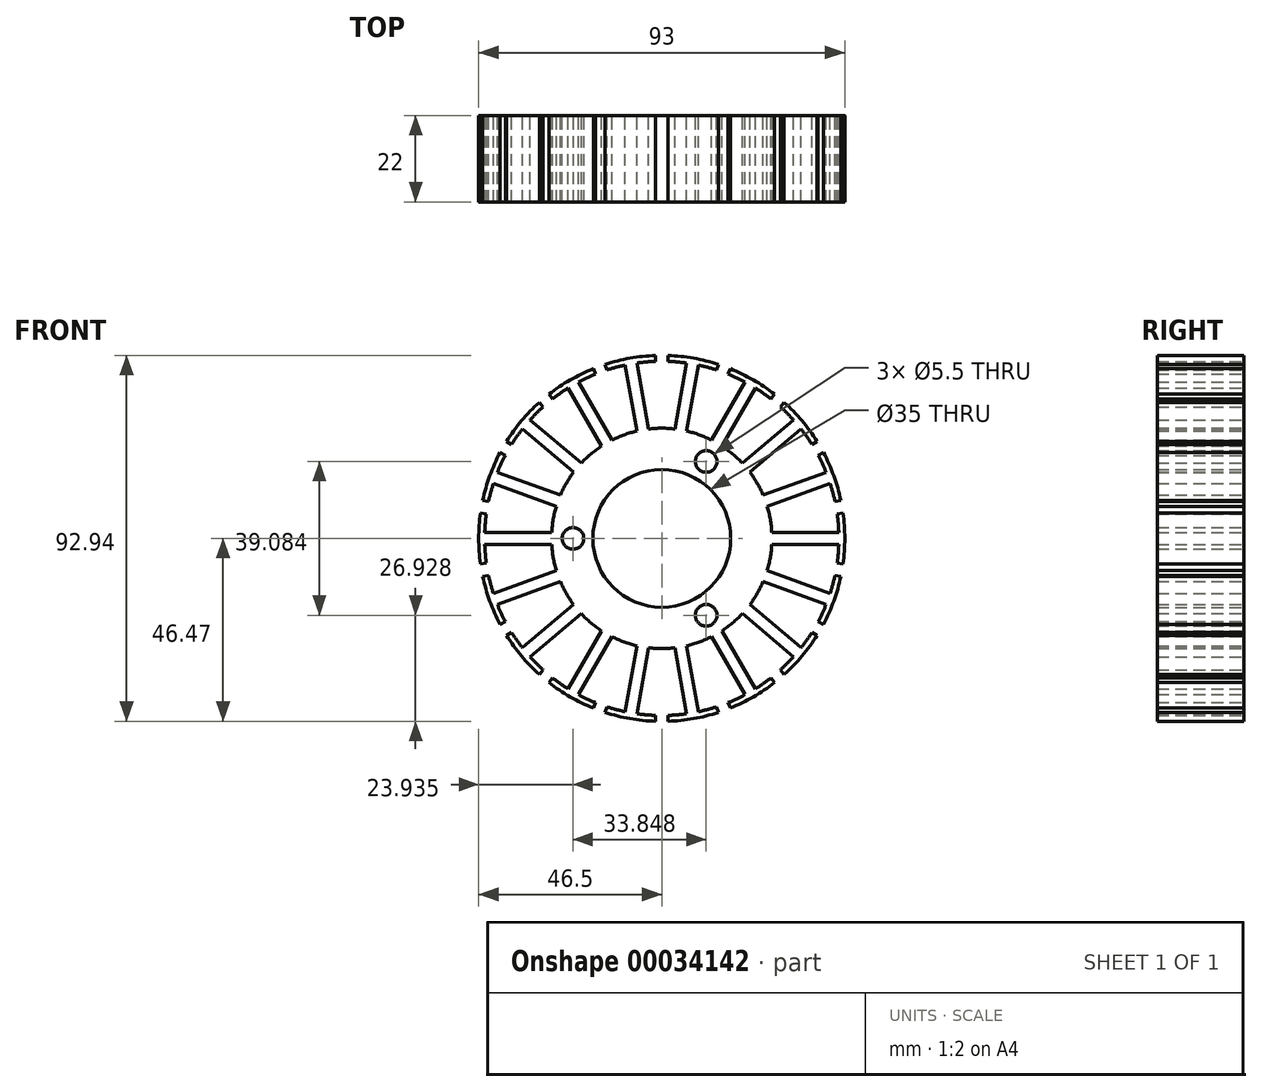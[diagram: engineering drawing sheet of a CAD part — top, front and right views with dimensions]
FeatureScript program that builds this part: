
annotation { "Feature Type Name" : "Feature", "Feature Type Description" : "" }
export const myFeature = defineFeature(function(context is Context, id is Id, definition is map)
    precondition{}
    {
        {
            var Q0;
            Q0=qCreatedBy(makeId("Front.planeOp"),FACE);
            var sketch = newSketch(context, id + "F0", { "sketchPlane" : qUnion([Q0])});
            skCircle(sketch, "E0", {"center": v(0, 0) * mm, "radius": 17.5 * mm});
            skArc(sketch, "E1", {"start": v(-46.04, 6.5) * mm, "mid": v(-46.5, 0) * mm, "end": v(-46.04, -6.5) * mm});
            skArc(sketch, "E2", {"start": v(-27.96, -1.5) * mm, "mid": v(-27.57, -4.86) * mm, "end": v(-26.79, -8.15) * mm});
            skLineSegment(sketch, "E3", {"start": v(-27.96, 1.5) * mm, "end": v(-44.97, 1.5) * mm});
            skLineSegment(sketch, "E4", {"start": v(-27.96, -1.5) * mm, "end": v(-44.97, -1.5) * mm});
            skArc(sketch, "E5", {"start": v(-44.56, 6.25) * mm, "mid": v(-44.83, 3.88) * mm, "end": v(-44.97, 1.5) * mm});
            skLineSegment(sketch, "E6", {"start": v(-46.04, 6.5) * mm, "end": v(-44.56, 6.25) * mm});
            skLineSegment(sketch, "E7", {"start": v(-46.04, -6.5) * mm, "end": v(-44.56, -6.25) * mm});
            skArc(sketch, "E8.trimOffspring", {"start": v(-44.97, -1.5) * mm, "mid": v(-44.83, -3.88) * mm, "end": v(-44.56, -6.25) * mm});
            skLineSegment(sketch, "E9.1.0", {"start": v(-26.79, 8.15) * mm, "end": v(-42.78, 13.97) * mm});
            skArc(sketch, "E9.1.1", {"start": v(-39.74, 21.11) * mm, "mid": v(-40.8, 18.98) * mm, "end": v(-41.75, 16.8) * mm});
            skArc(sketch, "E9.1.2", {"start": v(-42.78, 13.97) * mm, "mid": v(-43.46, 11.69) * mm, "end": v(-44.01, 9.37) * mm});
            skLineSegment(sketch, "E9.1.3", {"start": v(-25.76, 10.97) * mm, "end": v(-41.75, 16.8) * mm});
            skArc(sketch, "E9.1.4", {"start": v(-41.04, 21.86) * mm, "mid": v(-43.7, 15.9) * mm, "end": v(-45.49, 9.64) * mm});
            skLineSegment(sketch, "E9.1.5", {"start": v(-41.04, 21.86) * mm, "end": v(-39.74, 21.11) * mm});
            skLineSegment(sketch, "E9.1.6", {"start": v(-45.49, 9.64) * mm, "end": v(-44.01, 9.37) * mm});
            skLineSegment(sketch, "E9.2.0", {"start": v(-22.38, 16.82) * mm, "end": v(-35.42, 27.76) * mm});
            skArc(sketch, "E9.2.1", {"start": v(-30.12, 33.43) * mm, "mid": v(-31.85, 31.8) * mm, "end": v(-33.49, 30.06) * mm});
            skArc(sketch, "E9.2.2", {"start": v(-35.42, 27.76) * mm, "mid": v(-36.84, 25.85) * mm, "end": v(-38.16, 23.86) * mm});
            skLineSegment(sketch, "E9.2.3", {"start": v(-20.45, 19.12) * mm, "end": v(-33.49, 30.06) * mm});
            skArc(sketch, "E9.2.4", {"start": v(-31.1, 34.58) * mm, "mid": v(-35.62, 29.89) * mm, "end": v(-39.45, 24.62) * mm});
            skLineSegment(sketch, "E9.2.5", {"start": v(-31.1, 34.58) * mm, "end": v(-30.12, 33.43) * mm});
            skLineSegment(sketch, "E9.2.6", {"start": v(-39.45, 24.62) * mm, "end": v(-38.16, 23.86) * mm});
            skLineSegment(sketch, "E9.3.0", {"start": v(-15.28, 23.46) * mm, "end": v(-23.79, 38.2) * mm});
            skArc(sketch, "E9.3.1", {"start": v(-16.87, 41.72) * mm, "mid": v(-19.06, 40.77) * mm, "end": v(-21.19, 39.7) * mm});
            skArc(sketch, "E9.3.2", {"start": v(-23.79, 38.2) * mm, "mid": v(-25.78, 36.89) * mm, "end": v(-27.7, 35.47) * mm});
            skLineSegment(sketch, "E9.3.3", {"start": v(-12.68, 24.96) * mm, "end": v(-21.19, 39.7) * mm});
            skArc(sketch, "E9.3.4", {"start": v(-17.4, 43.12) * mm, "mid": v(-23.25, 40.27) * mm, "end": v(-28.65, 36.62) * mm});
            skLineSegment(sketch, "E9.3.5", {"start": v(-17.4, 43.12) * mm, "end": v(-16.87, 41.72) * mm});
            skLineSegment(sketch, "E9.3.6", {"start": v(-28.65, 36.62) * mm, "end": v(-27.7, 35.47) * mm});
            skLineSegment(sketch, "E9.4.0", {"start": v(-6.33, 27.27) * mm, "end": v(-9.29, 44.03) * mm});
            skArc(sketch, "E9.4.1", {"start": v(-1.58, 44.97) * mm, "mid": v(-3.96, 44.83) * mm, "end": v(-6.33, 44.55) * mm});
            skArc(sketch, "E9.4.2", {"start": v(-9.29, 44.03) * mm, "mid": v(-11.6, 43.48) * mm, "end": v(-13.9, 42.8) * mm});
            skLineSegment(sketch, "E9.4.3", {"start": v(-3.38, 27.8) * mm, "end": v(-6.33, 44.55) * mm});
            skArc(sketch, "E9.4.4", {"start": v(-1.6, 46.47) * mm, "mid": v(-8.07, 45.8) * mm, "end": v(-14.4, 44.22) * mm});
            skLineSegment(sketch, "E9.4.5", {"start": v(-1.6, 46.47) * mm, "end": v(-1.58, 44.97) * mm});
            skLineSegment(sketch, "E9.4.6", {"start": v(-14.4, 44.22) * mm, "end": v(-13.9, 42.8) * mm});
            skLineSegment(sketch, "E9.5.0", {"start": v(3.38, 27.8) * mm, "end": v(6.33, 44.55) * mm});
            skArc(sketch, "E9.5.1", {"start": v(13.9, 42.8) * mm, "mid": v(11.6, 43.48) * mm, "end": v(9.29, 44.03) * mm});
            skArc(sketch, "E9.5.2", {"start": v(6.33, 44.55) * mm, "mid": v(3.96, 44.83) * mm, "end": v(1.58, 44.97) * mm});
            skLineSegment(sketch, "E9.5.3", {"start": v(6.33, 27.27) * mm, "end": v(9.29, 44.03) * mm});
            skArc(sketch, "E9.5.4", {"start": v(14.4, 44.22) * mm, "mid": v(8.07, 45.8) * mm, "end": v(1.6, 46.47) * mm});
            skLineSegment(sketch, "E9.5.5", {"start": v(14.4, 44.22) * mm, "end": v(13.9, 42.8) * mm});
            skLineSegment(sketch, "E9.5.6", {"start": v(1.6, 46.47) * mm, "end": v(1.58, 44.97) * mm});
            skLineSegment(sketch, "E9.6.0", {"start": v(12.68, 24.96) * mm, "end": v(21.19, 39.7) * mm});
            skArc(sketch, "E9.6.1", {"start": v(27.7, 35.47) * mm, "mid": v(25.78, 36.89) * mm, "end": v(23.79, 38.2) * mm});
            skArc(sketch, "E9.6.2", {"start": v(21.19, 39.7) * mm, "mid": v(19.06, 40.77) * mm, "end": v(16.87, 41.72) * mm});
            skLineSegment(sketch, "E9.6.3", {"start": v(15.28, 23.46) * mm, "end": v(23.79, 38.2) * mm});
            skArc(sketch, "E9.6.4", {"start": v(28.65, 36.62) * mm, "mid": v(23.25, 40.27) * mm, "end": v(17.4, 43.12) * mm});
            skLineSegment(sketch, "E9.6.5", {"start": v(28.65, 36.62) * mm, "end": v(27.7, 35.47) * mm});
            skLineSegment(sketch, "E9.6.6", {"start": v(17.4, 43.12) * mm, "end": v(16.87, 41.72) * mm});
            skLineSegment(sketch, "E9.7.0", {"start": v(20.45, 19.12) * mm, "end": v(33.49, 30.06) * mm});
            skArc(sketch, "E9.7.1", {"start": v(38.16, 23.86) * mm, "mid": v(36.84, 25.85) * mm, "end": v(35.42, 27.76) * mm});
            skArc(sketch, "E9.7.2", {"start": v(33.49, 30.06) * mm, "mid": v(31.85, 31.8) * mm, "end": v(30.12, 33.43) * mm});
            skLineSegment(sketch, "E9.7.3", {"start": v(22.38, 16.82) * mm, "end": v(35.42, 27.76) * mm});
            skArc(sketch, "E9.7.4", {"start": v(39.45, 24.62) * mm, "mid": v(35.62, 29.89) * mm, "end": v(31.1, 34.58) * mm});
            skLineSegment(sketch, "E9.7.5", {"start": v(39.45, 24.62) * mm, "end": v(38.16, 23.86) * mm});
            skLineSegment(sketch, "E9.7.6", {"start": v(31.1, 34.58) * mm, "end": v(30.12, 33.43) * mm});
            skLineSegment(sketch, "E9.8.0", {"start": v(25.76, 10.97) * mm, "end": v(41.75, 16.8) * mm});
            skArc(sketch, "E9.8.1", {"start": v(44.01, 9.37) * mm, "mid": v(43.46, 11.69) * mm, "end": v(42.78, 13.97) * mm});
            skArc(sketch, "E9.8.2", {"start": v(41.75, 16.8) * mm, "mid": v(40.8, 18.98) * mm, "end": v(39.74, 21.11) * mm});
            skLineSegment(sketch, "E9.8.3", {"start": v(26.79, 8.15) * mm, "end": v(42.78, 13.97) * mm});
            skArc(sketch, "E9.8.4", {"start": v(45.49, 9.64) * mm, "mid": v(43.7, 15.9) * mm, "end": v(41.04, 21.86) * mm});
            skLineSegment(sketch, "E9.8.5", {"start": v(45.49, 9.64) * mm, "end": v(44.01, 9.37) * mm});
            skLineSegment(sketch, "E9.8.6", {"start": v(41.04, 21.86) * mm, "end": v(39.74, 21.11) * mm});
            skLineSegment(sketch, "E9.9.0", {"start": v(27.96, 1.5) * mm, "end": v(44.97, 1.5) * mm});
            skArc(sketch, "E9.9.1", {"start": v(44.56, -6.25) * mm, "mid": v(44.83, -3.88) * mm, "end": v(44.97, -1.5) * mm});
            skArc(sketch, "E9.9.2", {"start": v(44.97, 1.5) * mm, "mid": v(44.83, 3.88) * mm, "end": v(44.56, 6.25) * mm});
            skLineSegment(sketch, "E9.9.3", {"start": v(27.96, -1.5) * mm, "end": v(44.97, -1.5) * mm});
            skArc(sketch, "E9.9.4", {"start": v(46.04, -6.5) * mm, "mid": v(46.5, 0) * mm, "end": v(46.04, 6.5) * mm});
            skLineSegment(sketch, "E9.9.5", {"start": v(46.04, -6.5) * mm, "end": v(44.56, -6.25) * mm});
            skLineSegment(sketch, "E9.9.6", {"start": v(46.04, 6.5) * mm, "end": v(44.56, 6.25) * mm});
            skLineSegment(sketch, "E9.10.0", {"start": v(26.79, -8.15) * mm, "end": v(42.78, -13.97) * mm});
            skArc(sketch, "E9.10.1", {"start": v(39.74, -21.11) * mm, "mid": v(40.8, -18.98) * mm, "end": v(41.75, -16.8) * mm});
            skArc(sketch, "E9.10.2", {"start": v(42.78, -13.97) * mm, "mid": v(43.46, -11.69) * mm, "end": v(44.01, -9.37) * mm});
            skLineSegment(sketch, "E9.10.3", {"start": v(25.76, -10.97) * mm, "end": v(41.75, -16.8) * mm});
            skArc(sketch, "E9.10.4", {"start": v(41.04, -21.86) * mm, "mid": v(43.7, -15.9) * mm, "end": v(45.49, -9.64) * mm});
            skLineSegment(sketch, "E9.10.5", {"start": v(41.04, -21.86) * mm, "end": v(39.74, -21.11) * mm});
            skLineSegment(sketch, "E9.10.6", {"start": v(45.49, -9.64) * mm, "end": v(44.01, -9.37) * mm});
            skLineSegment(sketch, "E9.11.0", {"start": v(22.38, -16.82) * mm, "end": v(35.42, -27.76) * mm});
            skArc(sketch, "E9.11.1", {"start": v(30.12, -33.43) * mm, "mid": v(31.85, -31.8) * mm, "end": v(33.49, -30.06) * mm});
            skArc(sketch, "E9.11.2", {"start": v(35.42, -27.76) * mm, "mid": v(36.84, -25.85) * mm, "end": v(38.16, -23.86) * mm});
            skLineSegment(sketch, "E9.11.3", {"start": v(20.45, -19.12) * mm, "end": v(33.49, -30.06) * mm});
            skArc(sketch, "E9.11.4", {"start": v(31.1, -34.58) * mm, "mid": v(35.62, -29.89) * mm, "end": v(39.45, -24.62) * mm});
            skLineSegment(sketch, "E9.11.5", {"start": v(31.1, -34.58) * mm, "end": v(30.12, -33.43) * mm});
            skLineSegment(sketch, "E9.11.6", {"start": v(39.45, -24.62) * mm, "end": v(38.16, -23.86) * mm});
            skLineSegment(sketch, "E9.12.0", {"start": v(15.28, -23.46) * mm, "end": v(23.79, -38.2) * mm});
            skArc(sketch, "E9.12.1", {"start": v(16.87, -41.72) * mm, "mid": v(19.06, -40.77) * mm, "end": v(21.19, -39.7) * mm});
            skArc(sketch, "E9.12.2", {"start": v(23.79, -38.2) * mm, "mid": v(25.78, -36.89) * mm, "end": v(27.7, -35.47) * mm});
            skLineSegment(sketch, "E9.12.3", {"start": v(12.68, -24.96) * mm, "end": v(21.19, -39.7) * mm});
            skArc(sketch, "E9.12.4", {"start": v(17.4, -43.12) * mm, "mid": v(23.25, -40.27) * mm, "end": v(28.65, -36.62) * mm});
            skLineSegment(sketch, "E9.12.5", {"start": v(17.4, -43.12) * mm, "end": v(16.87, -41.72) * mm});
            skLineSegment(sketch, "E9.12.6", {"start": v(28.65, -36.62) * mm, "end": v(27.7, -35.47) * mm});
            skLineSegment(sketch, "E9.13.0", {"start": v(6.33, -27.27) * mm, "end": v(9.29, -44.03) * mm});
            skArc(sketch, "E9.13.1", {"start": v(1.58, -44.97) * mm, "mid": v(3.96, -44.83) * mm, "end": v(6.33, -44.55) * mm});
            skArc(sketch, "E9.13.2", {"start": v(9.29, -44.03) * mm, "mid": v(11.6, -43.48) * mm, "end": v(13.9, -42.8) * mm});
            skLineSegment(sketch, "E9.13.3", {"start": v(3.38, -27.8) * mm, "end": v(6.33, -44.55) * mm});
            skArc(sketch, "E9.13.4", {"start": v(1.6, -46.47) * mm, "mid": v(8.07, -45.8) * mm, "end": v(14.4, -44.22) * mm});
            skLineSegment(sketch, "E9.13.5", {"start": v(1.6, -46.47) * mm, "end": v(1.58, -44.97) * mm});
            skLineSegment(sketch, "E9.13.6", {"start": v(14.4, -44.22) * mm, "end": v(13.9, -42.8) * mm});
            skLineSegment(sketch, "E9.14.0", {"start": v(-3.38, -27.8) * mm, "end": v(-6.33, -44.55) * mm});
            skArc(sketch, "E9.14.1", {"start": v(-13.9, -42.8) * mm, "mid": v(-11.6, -43.48) * mm, "end": v(-9.29, -44.03) * mm});
            skArc(sketch, "E9.14.2", {"start": v(-6.33, -44.55) * mm, "mid": v(-3.96, -44.83) * mm, "end": v(-1.58, -44.97) * mm});
            skLineSegment(sketch, "E9.14.3", {"start": v(-6.33, -27.27) * mm, "end": v(-9.29, -44.03) * mm});
            skArc(sketch, "E9.14.4", {"start": v(-14.4, -44.22) * mm, "mid": v(-8.07, -45.8) * mm, "end": v(-1.6, -46.47) * mm});
            skLineSegment(sketch, "E9.14.5", {"start": v(-14.4, -44.22) * mm, "end": v(-13.9, -42.8) * mm});
            skLineSegment(sketch, "E9.14.6", {"start": v(-1.6, -46.47) * mm, "end": v(-1.58, -44.97) * mm});
            skLineSegment(sketch, "E9.15.0", {"start": v(-12.68, -24.96) * mm, "end": v(-21.19, -39.7) * mm});
            skArc(sketch, "E9.15.1", {"start": v(-27.7, -35.47) * mm, "mid": v(-25.78, -36.89) * mm, "end": v(-23.79, -38.2) * mm});
            skArc(sketch, "E9.15.2", {"start": v(-21.19, -39.7) * mm, "mid": v(-19.06, -40.77) * mm, "end": v(-16.87, -41.72) * mm});
            skLineSegment(sketch, "E9.15.3", {"start": v(-15.28, -23.46) * mm, "end": v(-23.79, -38.2) * mm});
            skArc(sketch, "E9.15.4", {"start": v(-28.65, -36.62) * mm, "mid": v(-23.25, -40.27) * mm, "end": v(-17.4, -43.12) * mm});
            skLineSegment(sketch, "E9.15.5", {"start": v(-28.65, -36.62) * mm, "end": v(-27.7, -35.47) * mm});
            skLineSegment(sketch, "E9.15.6", {"start": v(-17.4, -43.12) * mm, "end": v(-16.87, -41.72) * mm});
            skLineSegment(sketch, "E9.16.0", {"start": v(-20.45, -19.12) * mm, "end": v(-33.49, -30.06) * mm});
            skArc(sketch, "E9.16.1", {"start": v(-38.16, -23.86) * mm, "mid": v(-36.84, -25.85) * mm, "end": v(-35.42, -27.76) * mm});
            skArc(sketch, "E9.16.2", {"start": v(-33.49, -30.06) * mm, "mid": v(-31.85, -31.8) * mm, "end": v(-30.12, -33.43) * mm});
            skLineSegment(sketch, "E9.16.3", {"start": v(-22.38, -16.82) * mm, "end": v(-35.42, -27.76) * mm});
            skArc(sketch, "E9.16.4", {"start": v(-39.45, -24.62) * mm, "mid": v(-35.62, -29.89) * mm, "end": v(-31.1, -34.58) * mm});
            skLineSegment(sketch, "E9.16.5", {"start": v(-39.45, -24.62) * mm, "end": v(-38.16, -23.86) * mm});
            skLineSegment(sketch, "E9.16.6", {"start": v(-31.1, -34.58) * mm, "end": v(-30.12, -33.43) * mm});
            skLineSegment(sketch, "E9.17.0", {"start": v(-25.76, -10.97) * mm, "end": v(-41.75, -16.8) * mm});
            skArc(sketch, "E9.17.1", {"start": v(-44.01, -9.37) * mm, "mid": v(-43.46, -11.69) * mm, "end": v(-42.78, -13.97) * mm});
            skArc(sketch, "E9.17.2", {"start": v(-41.75, -16.8) * mm, "mid": v(-40.8, -18.98) * mm, "end": v(-39.74, -21.11) * mm});
            skLineSegment(sketch, "E9.17.3", {"start": v(-26.79, -8.15) * mm, "end": v(-42.78, -13.97) * mm});
            skArc(sketch, "E9.17.4", {"start": v(-45.49, -9.64) * mm, "mid": v(-43.7, -15.9) * mm, "end": v(-41.04, -21.86) * mm});
            skLineSegment(sketch, "E9.17.5", {"start": v(-45.49, -9.64) * mm, "end": v(-44.01, -9.37) * mm});
            skLineSegment(sketch, "E9.17.6", {"start": v(-41.04, -21.86) * mm, "end": v(-39.74, -21.11) * mm});
            skLineSegment(sketch, "E9.anchor1", {"start": v(0, 0) * mm, "end": v(-46.04, 6.5) * mm, "construction": true});
            skLineSegment(sketch, "E9.anchor2", {"start": v(0, 0) * mm, "end": v(-45.49, -9.64) * mm, "construction": true});
            skArc(sketch, "E10.trimOffspring", {"start": v(-25.76, -10.97) * mm, "mid": v(-24.25, -14) * mm, "end": v(-22.38, -16.82) * mm});
            skArc(sketch, "E11.trimOffspring", {"start": v(-20.45, -19.12) * mm, "mid": v(-18, -21.45) * mm, "end": v(-15.28, -23.46) * mm});
            skArc(sketch, "E12.trimOffspring", {"start": v(-12.68, -24.96) * mm, "mid": v(-9.58, -26.31) * mm, "end": v(-6.33, -27.27) * mm});
            skArc(sketch, "E13.trimOffspring", {"start": v(-3.38, -27.8) * mm, "mid": v(0, -28) * mm, "end": v(3.38, -27.8) * mm});
            skArc(sketch, "E14.trimOffspring", {"start": v(6.33, -27.27) * mm, "mid": v(9.58, -26.31) * mm, "end": v(12.68, -24.96) * mm});
            skArc(sketch, "E15.trimOffspring", {"start": v(15.28, -23.46) * mm, "mid": v(18, -21.45) * mm, "end": v(20.45, -19.12) * mm});
            skArc(sketch, "E16.trimOffspring", {"start": v(22.38, -16.82) * mm, "mid": v(24.25, -14) * mm, "end": v(25.76, -10.97) * mm});
            skArc(sketch, "E17.trimOffspring", {"start": v(26.79, -8.15) * mm, "mid": v(27.57, -4.86) * mm, "end": v(27.96, -1.5) * mm});
            skArc(sketch, "E18.trimOffspring", {"start": v(27.96, 1.5) * mm, "mid": v(27.57, 4.86) * mm, "end": v(26.79, 8.15) * mm});
            skArc(sketch, "E19.trimOffspring", {"start": v(25.76, 10.97) * mm, "mid": v(24.25, 14) * mm, "end": v(22.38, 16.82) * mm});
            skArc(sketch, "E20.trimOffspring", {"start": v(20.45, 19.12) * mm, "mid": v(18, 21.45) * mm, "end": v(15.28, 23.46) * mm});
            skArc(sketch, "E21.trimOffspring", {"start": v(12.68, 24.96) * mm, "mid": v(9.58, 26.31) * mm, "end": v(6.33, 27.27) * mm});
            skArc(sketch, "E22.trimOffspring", {"start": v(3.38, 27.8) * mm, "mid": v(0, 28) * mm, "end": v(-3.38, 27.8) * mm});
            skArc(sketch, "E23.trimOffspring", {"start": v(-6.33, 27.27) * mm, "mid": v(-9.58, 26.31) * mm, "end": v(-12.68, 24.96) * mm});
            skArc(sketch, "E24.trimOffspring", {"start": v(-15.28, 23.46) * mm, "mid": v(-18, 21.45) * mm, "end": v(-20.45, 19.12) * mm});
            skArc(sketch, "E25.trimOffspring", {"start": v(-22.38, 16.82) * mm, "mid": v(-24.25, 14) * mm, "end": v(-25.76, 10.97) * mm});
            skArc(sketch, "E26.trimOffspring", {"start": v(-26.79, 8.15) * mm, "mid": v(-27.57, 4.86) * mm, "end": v(-27.96, 1.5) * mm});
            skCircle(sketch, "E27", {"center": v(-22.57, 0) * mm, "radius": 2.75 * mm});
            skCircle(sketch, "E28.1.0", {"center": v(11.28, -19.54) * mm, "radius": 2.75 * mm});
            skCircle(sketch, "E28.2.0", {"center": v(11.28, 19.54) * mm, "radius": 2.75 * mm});
            skSolve(sketch);
        }
        {
            var Q0;
            Q0 = qSketchRegion(id + "F0", true);
            extrude(context, id + "F1", {"entities" : qUnion([Q0]), "endBound" : BoundingType.SYMMETRIC, "depth" : 22 * mm});
        }
    });
